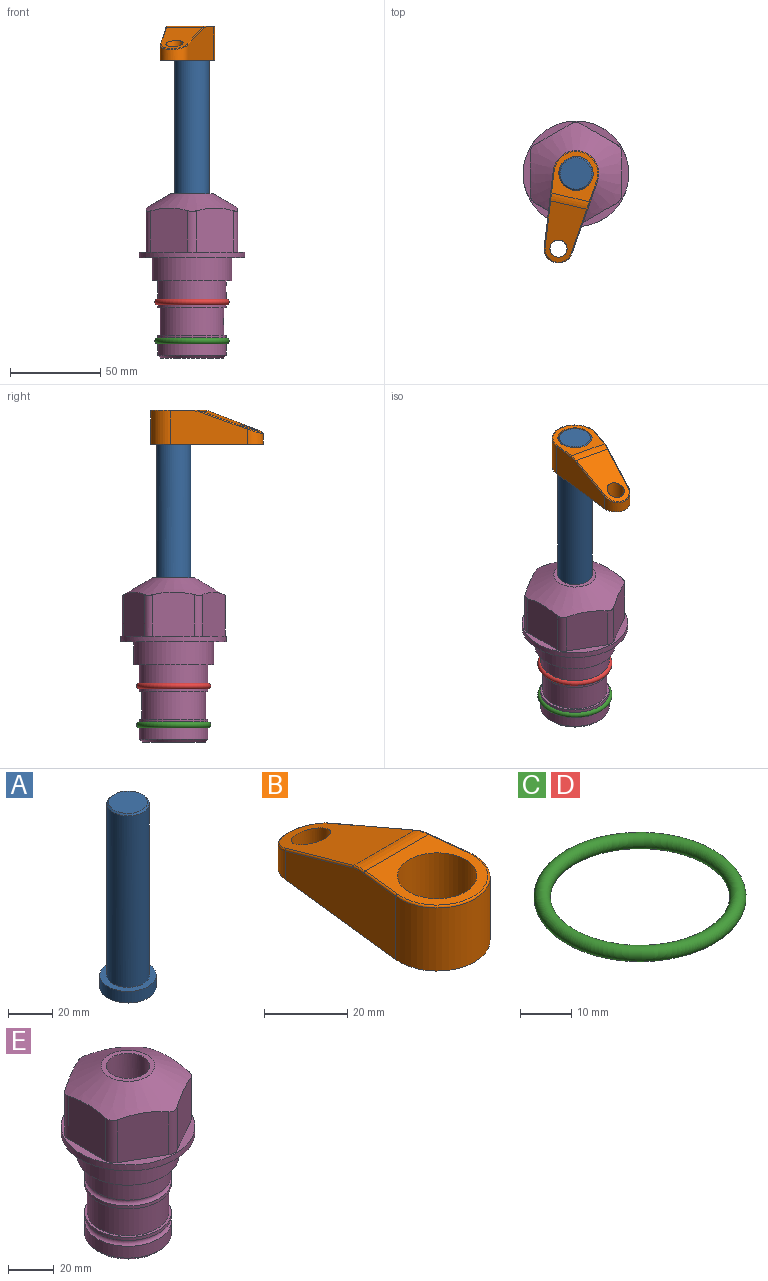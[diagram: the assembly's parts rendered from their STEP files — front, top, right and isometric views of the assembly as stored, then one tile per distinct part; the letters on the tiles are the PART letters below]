
ASSEMBLY  parts=5 mates=3
PART A: 6 faces, bbox 25.4x25.4x101.6 mm
  f0: plane 17.46x17.46mm, normal (0,0,1), area 239.5mm2, adj f5
  f1: plane 25.4x25.4mm, normal (0,0,-1), area 506.7mm2, adj f2
  f2: cylinder r=12.7mm len=25.4mm, axis (0,0,1), area 506.7mm2, adj f1,f3
  f3: plane 25.4x25.4mm, normal (0,0,1), area 221.7mm2, adj f2,f4
  f4: cylinder r=9.53mm len=94.46mm, axis (0,0,1), area 5653mm2, adj f3,f5
  f5: cone r=8.73mm half-angle=45deg, axis (0,0,-1), area 64.4mm2, adj f0,f4
PART B: 44 faces, bbox 27.5x64.5x19.1 mm
  f0: plane 2.3x0.95mm, normal (0,0,-1), area 1mm2, adj f25,f30,f34
  f1: plane 63.5x25.4mm, normal (0,0,-1), area 561.7mm2, adj f2,f3,f4,f5,f6,f7,f19,f20
  f2: cylinder r=12.7mm len=25.4mm, axis (0,0,-1), area 792.2mm2, adj f1,f3,f5,f13
  f3: plane 42.33x18.54mm, normal (0.99,0.11,0), area 647mm2, adj f1,f2,f4,f11,f12,f14
  f4: cylinder r=7.94mm len=15.78mm, axis (0,0,-1), area 158.6mm2, adj f1,f3,f5,f16
  f5: plane 42.33x18.54mm, normal (-0.99,0.11,0), area 647mm2, adj f1,f2,f4,f15,f17,f18
  f6: cylinder r=9.53mm len=19.05mm, axis (0,0,-1), area 1140.1mm2, adj f1,f8
  f7: cylinder r=4.76mm len=10.98mm, axis (0,0,-1), area 276.1mm2, adj f1,f9
  f8: plane 25.83x24.38mm, normal (0,0,1), area 262.2mm2, adj f6,f10,f11,f13,f15
  f9: plane 32.49x20.55mm, normal (0,0.34,0.94), area 489.9mm2, adj f7,f10,f14,f16,f18
  f10: cylinder r=12.7mm len=21.49mm, axis (-1,0,0), area 93.2mm2, adj f8,f9,f12,f17
  f11: cylinder r=0.51mm len=12.34mm, axis (0.11,-0.99,0), area 9.9mm2, adj f3,f8,f12,f13
  f12: bspline ~7.62x1.64mm, area 3.5mm2, adj f3,f10,f11,f14
  f13: torus R=12.19mm, axis (0,0,1), area 33.6mm2, adj f2,f8,f11,f15
  f14: cylinder r=0.51mm len=26.01mm, axis (0.1,-0.93,0.34), area 21.6mm2, adj f3,f9,f12,f16
  f15: cylinder r=0.51mm len=12.34mm, axis (0.11,0.99,0), area 9.9mm2, adj f5,f8,f13,f17
  f16: bspline ~15.78x7.05mm, area 15.7mm2, adj f4,f9,f14,f18
  f17: bspline ~7.62x1.64mm, area 3.5mm2, adj f5,f10,f15,f18
  f18: cylinder r=0.51mm len=26.01mm, axis (0.1,0.93,-0.34), area 21.6mm2, adj f5,f9,f16,f17
  f19: plane 21.6x14.29mm, normal (-0.99,-0.11,0), area 242.6mm2, adj f1,f26,f28,f34,f36,f38
  f20: plane 21.6x14.29mm, normal (0.99,-0.11,0), area 242.6mm2, adj f1,f27,f29,f37,f39,f41
  f21: cylinder r=12.7mm len=14.29mm, axis (0,0,-1), area 173.2mm2, adj f1,f26,f27,f30,f31,f33
  f22: cylinder r=7.94mm len=7.63mm, axis (0,0,-1), area 53.8mm2, adj f1,f28,f29,f42
  f23: plane 2.3x0.95mm, normal (0,0,-1), area 1mm2, adj f25,f33,f37
  f24: plane 17.94x12.32mm, normal (0,-0.34,-0.94), area 191.2mm2, adj f25,f38,f41,f42
  f25: cylinder r=9.53mm len=12.93mm, axis (-1,0,0), area 37.5mm2, adj f0,f23,f24,f31,f36,f39
  f26: cylinder r=1.59mm len=14.29mm, axis (0,0,-1), area 49mm2, adj f1,f19,f21,f32
  f27: cylinder r=1.59mm len=14.29mm, axis (0,0,-1), area 49mm2, adj f1,f20,f21,f35
  f28: cylinder r=1.59mm len=7.28mm, axis (0,0,-1), area 22.1mm2, adj f1,f19,f22,f40
  f29: cylinder r=1.59mm len=7.28mm, axis (0,0,-1), area 22.1mm2, adj f1,f20,f22,f43
  f30: torus R=14.29mm, axis (0,0,1), area 5.8mm2, adj f0,f21,f31,f32
  f31: bspline ~11.06x2.73mm, area 20.8mm2, adj f21,f25,f30,f33
  f32: sphere r=1.59mm, area 5.4mm2, adj f26,f30,f34
  f33: torus R=14.29mm, axis (0,0,1), area 5.8mm2, adj f21,f23,f31,f35
  f34: cylinder r=1.59mm len=1.68mm, axis (-0.11,0.99,0), area 2.4mm2, adj f0,f19,f32,f36
  f35: sphere r=1.59mm, area 5.4mm2, adj f27,f33,f37
  f36: bspline ~5.82x2.33mm, area 7.7mm2, adj f19,f25,f34,f38
  f37: cylinder r=1.59mm len=1.68mm, axis (0.11,0.99,0), area 2.4mm2, adj f20,f23,f35,f39
  f38: cylinder r=1.59mm len=18.33mm, axis (0.1,-0.93,0.34), area 46.7mm2, adj f19,f24,f36,f40
  f39: bspline ~5.82x2.33mm, area 7.7mm2, adj f20,f25,f37,f41
  f40: sphere r=1.59mm, area 3.6mm2, adj f28,f38,f42
  f41: cylinder r=1.59mm len=18.33mm, axis (0.1,0.93,-0.34), area 46.7mm2, adj f20,f24,f39,f43
  f42: bspline ~8.31x1.84mm, area 15.3mm2, adj f22,f24,f40,f43
  f43: sphere r=1.59mm, area 3.6mm2, adj f29,f41,f42
PART C: 1 faces, bbox 44.7x44.7x3.2 mm
  f0: torus R=19.05mm, axis (0,0,1), area 1193.9mm2
PART D: same geometry as C
PART E: 36 faces, bbox 58.7x58.7x91.2 mm
  f0: cylinder r=17.78mm len=35.56mm, axis (0,0,1), area 1670.8mm2, adj f23,f24,f31
  f1: cylinder r=19.05mm len=38.1mm, axis (0,0,1), area 1191.9mm2, adj f26,f27,f30
  f2: plane 58.66x58.66mm, normal (0,0,-1), area 1150.6mm2, adj f3,f28
  f3: cylinder r=29.33mm len=58.66mm, axis (0,0,-1), area 585.1mm2, adj f2,f4
  f4: plane 58.66x58.66mm, normal (0,0,1), area 475.9mm2, adj f3,f5,f6,f7,f8,f9,f10,f11
  f5: plane 24.5x20.32mm, normal (-0.5,0.87,0), area 562.8mm2, adj f4,f15,f16,f17
  f6: plane 24.5x20.32mm, normal (0.5,0.87,0), area 562.8mm2, adj f4,f14,f15,f17
  f7: plane 24.5x23.48mm, normal (1,0,0), area 562.8mm2, adj f4,f13,f14,f17
  f8: plane 24.5x20.32mm, normal (0.5,-0.87,0), area 562.8mm2, adj f4,f12,f13,f17
  f9: plane 24.5x20.32mm, normal (-0.5,-0.87,0), area 562.8mm2, adj f4,f11,f12,f17
  f10: plane 24.5x23.48mm, normal (-1,0,0), area 562.8mm2, adj f4,f11,f16,f17
  f11: cylinder r=5.08mm len=23.01mm, axis (0,0,-1), area 121.2mm2, adj f4,f9,f10,f17
  f12: cylinder r=5.08mm len=23.01mm, axis (0,0,-1), area 121.2mm2, adj f4,f8,f9,f17
  f13: cylinder r=5.08mm len=23.01mm, axis (0,0,-1), area 121.2mm2, adj f4,f7,f8,f17
  f14: cylinder r=5.08mm len=23.01mm, axis (0,0,-1), area 121.2mm2, adj f4,f6,f7,f17
  f15: cylinder r=5.08mm len=23.01mm, axis (0,0,-1), area 121.2mm2, adj f4,f5,f6,f17
  f16: cylinder r=5.08mm len=23.01mm, axis (0,0,-1), area 121.2mm2, adj f4,f5,f10,f17
  f17: cone r=11.73mm half-angle=60deg, axis (0,0,-1), area 2071.8mm2, adj f5,f6,f7,f8,f9,f10,f11,f12
  f18: plane 23.46x23.46mm, normal (0,0,1), area 147.4mm2, adj f17,f35
  f19: plane 34.93x34.93mm, normal (0,0,-1), area 958mm2, adj f29
  f20: cylinder r=19.05mm len=38.1mm, axis (0,0,1), area 760.1mm2, adj f21,f29
  f21: torus R=19.05mm, axis (0,0,1), area 565.3mm2, adj f20,f22
  f22: cylinder r=19.05mm len=38.1mm, axis (0,0,1), area 190mm2, adj f21,f23
  f23: plane 38.1x38.1mm, normal (0,0,1), area 146.9mm2, adj f0,f22
  f24: plane 38.1x38.1mm, normal (0,0,-1), area 146.9mm2, adj f0,f25
  f25: cylinder r=19.05mm len=38.1mm, axis (0,0,1), area 190mm2, adj f24,f26
  f26: torus R=19.05mm, axis (0,0,1), area 565.3mm2, adj f1,f25
  f27: plane 44.45x44.45mm, normal (0,0,-1), area 411.7mm2, adj f1,f28
  f28: cylinder r=22.23mm len=44.45mm, axis (0,0,1), area 1773.5mm2, adj f2,f27
  f29: cone r=19.05mm half-angle=45deg, axis (0,0,1), area 257.5mm2, adj f19,f20
  f30: cylinder r=3.17mm len=6.75mm, axis (-1,0,0), area 128mm2, adj f1,f33
  f31: cylinder r=3.17mm len=6.35mm, axis (-1,0,0), area 102.5mm2, adj f0,f33
  f32: plane 25.4x25.4mm, normal (0,0,1), area 506.7mm2, adj f33
  f33: cylinder r=12.7mm len=66.42mm, axis (0,0,-1), area 5236.2mm2, adj f30,f31,f32,f34
  f34: cone r=9.53mm half-angle=30deg, axis (0,0,-1), area 443.4mm2, adj f33,f35
  f35: cylinder r=9.53mm len=19.05mm, axis (0,0,-1), area 849mm2, adj f18,f34
PLACE A rot(axis=(0,0,-1),103.1deg) t=(0,0,55.11)mm
PLACE B rot(axis=(0,0,1),166.9deg) t=(0,0,109.72)mm
PLACE C t=(0,0,-21.59)mm
PLACE D at identity
PLACE E at identity fixed
MATE fastened C.f0 <-> E.f0  axis (0,0,1) through (0,0,-46.1)mm
MATE cylindrical A.f2 <-> E.f0  axis (0,0,1) through (0,0,80.75)mm
MATE fastened B.f2 <-> A.f2  axis (0,0,1) through (0,0,128.77)mm
